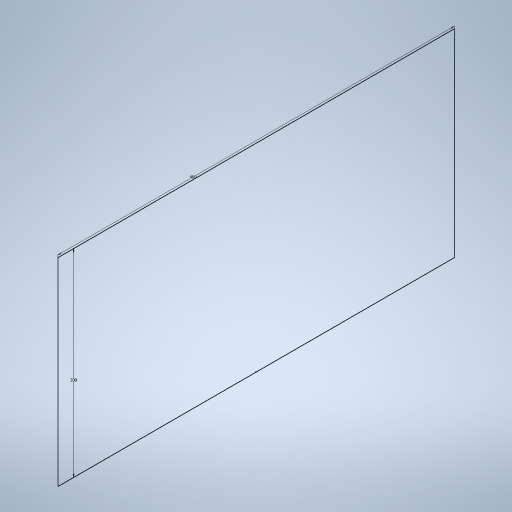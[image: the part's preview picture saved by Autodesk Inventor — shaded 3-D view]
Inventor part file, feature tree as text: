
AUTODESK INVENTOR PART (.ipt)
format: ipt  version: 2024.3 (Build 283343000, 343)  size: 233,984 bytes
history: native  units: mm
features: sketch x1
ambient origin geometry x8: Origin, YZ Plane, XZ Plane, XY Plane, X Axis, Y Axis, Z Axis, Center Point
feature tree (1):
  sketch  "Sketch1"  dims[d0=400.0mm d1=200.0mm]
